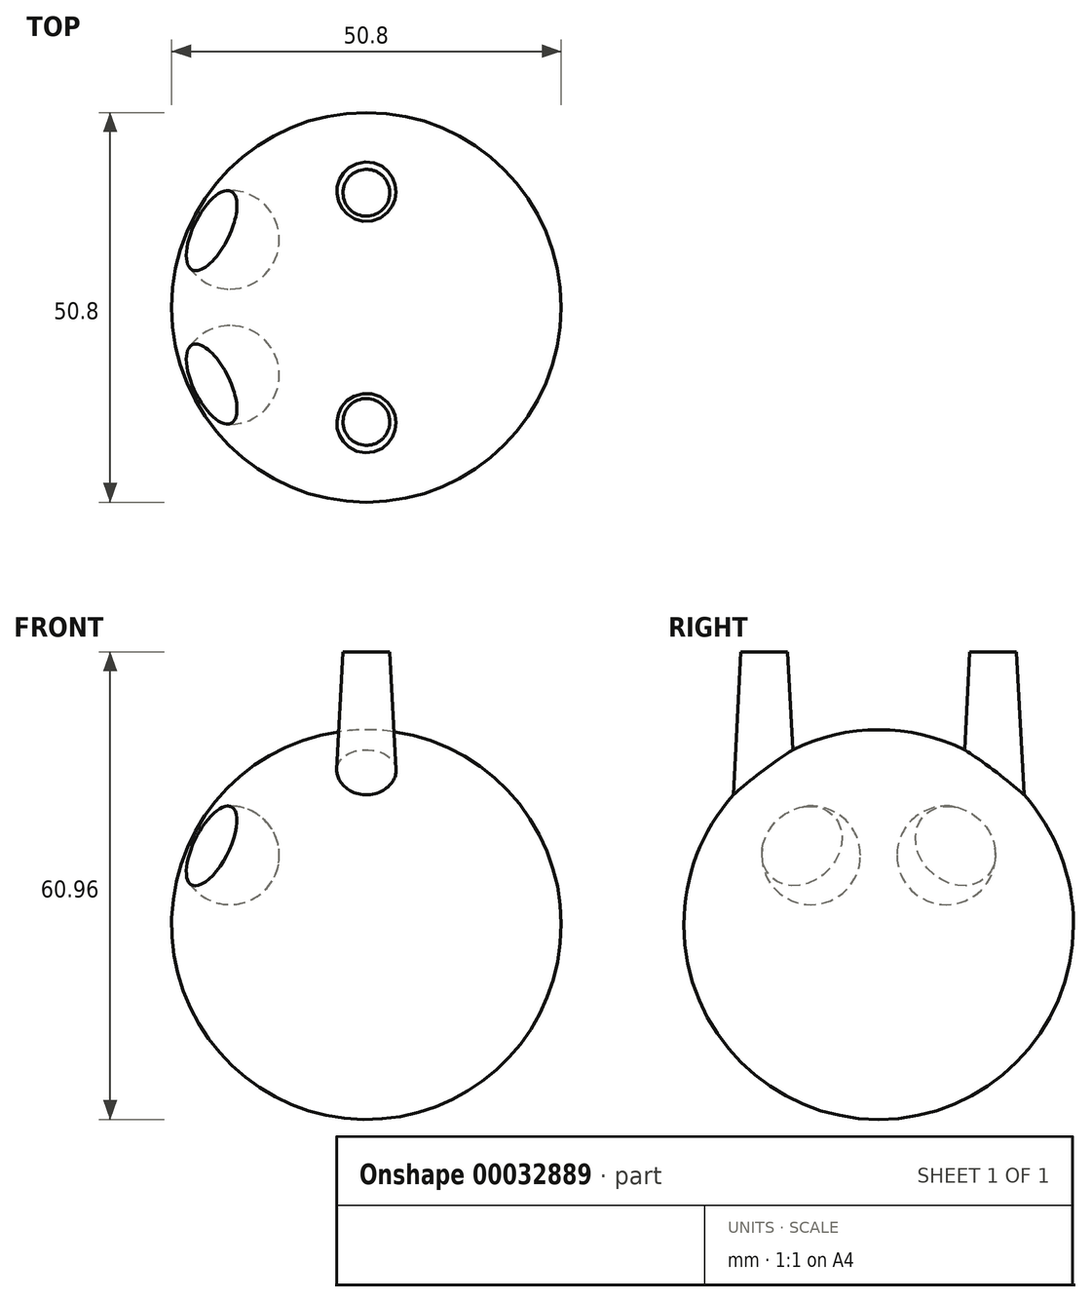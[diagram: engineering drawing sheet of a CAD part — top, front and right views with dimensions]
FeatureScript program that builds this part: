
annotation { "Feature Type Name" : "Feature", "Feature Type Description" : "" }
export const myFeature = defineFeature(function(context is Context, id is Id, definition is map)
    precondition{}
    {
        {
            var Q0;
            Q0=qCreatedBy(makeId("Right.planeOp"),FACE);
            var sketch = newSketch(context, id + "F0", { "sketchPlane" : qUnion([Q0])});
            skLineSegment(sketch, "E0", {"start": v(0, 0) * mm, "end": v(-25.4, 0) * mm});
            skLineSegment(sketch, "E1", {"start": v(-25.4, 0) * mm, "end": v(0, 0) * mm});
            skLineSegment(sketch, "E2", {"start": v(0, 0) * mm, "end": v(25.4, 0) * mm});
            skArc(sketch, "E3", {"start": v(25.4, 0) * mm, "mid": v(0, 25.4) * mm, "end": v(-25.4, 0) * mm});
            skPoint(sketch, "E4", {"position": v(0, 25.4) * mm});
            skSolve(sketch);
        }
        {
            var Q0;
            Q0 = qSketchRegion(id + "F0", true);
            var Q1;
            Q1=sQuery(id+"F0.wireOp",EDGE,"E2");
            revolve(context, id + "F1", {"entities" : qUnion([Q0]), "axis" : qUnion([Q1]), "revolveType" : RevolveType.FULL});
        }
        {
            var Q0;
            Q0=qCreatedBy(makeId("Right.planeOp"),FACE);
            cPlane(context, id + "F2", {"entities" : qUnion([Q0]), "cplaneType" : CPlaneType.OFFSET, "offset" : 17.78 * mm, "oppositeDirection" : true, "width" : 152.4 * mm, "height" : 152.4 * mm});
        }
        {
            var Q0;
            Q0=qCreatedBy(id+"F2.planeOp",FACE);
            var sketch = newSketch(context, id + "F3", { "sketchPlane" : qUnion([Q0])});
            skPoint(sketch, "E5.orphan", {"position": v(25.07, 9.03) * mm});
            skPoint(sketch, "E6.orphan", {"position": v(-25.07, 9.03) * mm});
            skPoint(sketch, "E7.orphan", {"position": v(0, 9.03) * mm});
            skLineSegment(sketch, "E8", {"start": v(2.39, 9.03) * mm, "end": v(-4.78, 9.03) * mm});
            skLineSegment(sketch, "E9", {"start": v(0, 9.03) * mm, "end": v(2.39, 9.03) * mm});
            skPoint(sketch, "E10.center.orphan", {"position": v(9.62, 9.03) * mm});
            skPoint(sketch, "E11", {"position": v(2.39, 9.03) * mm});
            skPoint(sketch, "E12", {"position": v(14.46, 9.03) * mm});
            skPoint(sketch, "E13.orphan", {"position": v(8.66, 9.03) * mm});
            skPoint(sketch, "E14.start.orphan", {"position": v(10.57, 9.03) * mm});
            skPoint(sketch, "E15.orphan", {"position": v(4.78, 9.03) * mm});
            skLineSegment(sketch, "E16", {"start": v(2.39, 9.03) * mm, "end": v(15.24, 9.03) * mm});
            skArc(sketch, "E17", {"start": v(15.24, 9.03) * mm, "mid": v(8.81, 15.45) * mm, "end": v(2.39, 9.03) * mm});
            skLineSegment(sketch, "E18", {"start": v(0, 9.03) * mm, "end": v(0, 14.03) * mm});
            skArc(sketch, "E19.MirrorCS", {"start": v(-15.24, 9.03) * mm, "mid": v(-8.81, 15.45) * mm, "end": v(-2.39, 9.03) * mm});
            skLineSegment(sketch, "E20", {"start": v(-15.24, 9.03) * mm, "end": v(-4.78, 9.03) * mm});
            skSolve(sketch);
        }
        {
            var Q0;
            Q0 = qSketchRegion(id + "F3", true);
            var Q1;
            Q1=sQuery(id+"F3.wireOp",EDGE,"E8");
            revolve(context, id + "F4", {"operationType" : NewBodyOperationType.REMOVE, "entities" : qUnion([Q0]), "axis" : qUnion([Q1]), "revolveType" : RevolveType.FULL, "oppositeDirection" : true});
        }
        {
            var Q0;
            Q0=qCreatedBy(makeId("Top.planeOp"),FACE);
            cPlane(context, id + "F5", {"entities" : qUnion([Q0]), "cplaneType" : CPlaneType.OFFSET, "offset" : 35.56 * mm, "width" : 152.4 * mm, "height" : 152.4 * mm});
        }
        {
            var Q0;
            Q0=qCreatedBy(id+"F5.planeOp",FACE);
            var sketch = newSketch(context, id + "F6", { "sketchPlane" : qUnion([Q0])});
            skLineSegment(sketch, "E21", {"start": v(0, 14.93) * mm, "end": v(0, 11) * mm});
            skLineSegment(sketch, "E22.MirrorCS", {"start": v(0, -14.93) * mm, "end": v(0, -11) * mm});
            skCircle(sketch, "E23", {"center": v(0, 14.93) * mm, "radius": 3.05 * mm});
            skLineSegment(sketch, "E24", {"start": v(0, 0) * mm, "end": v(10.18, 0) * mm});
            skCircle(sketch, "E25.MirrorC", {"center": v(0, -14.93) * mm, "radius": 3.05 * mm});
            skSolve(sketch);
        }
        {
            var Q0;
            Q0 = qSketchRegion(id + "F6", true);
            extrude(context, id + "F7", {"entities" : qUnion([Q0]), "operationType" : NewBodyOperationType.ADD, "oppositeDirection" : true, "depth" : 45.72 * mm, "hasDraft" : true, "draftAngle" : 3 * degree});
        }
    });
